# Revit family: OPUS-M
name_source: partatom
category: Mechanical Equipment
revit_build: Autodesk Revit 2015 (Build: 20140606_1530(x64)
units: mm (PartAtom-declared; Revit-internal decimal feet)

## types (2) — shared parameters
Catalogue Pages = http://www.nuaire.info
Discharge Spigot Diameter = 200 mm  [stored 0.656168 ft]
Electrical Phase = 1
Extract Spigot (Large) Diameter = 150 mm
Extract Spigot (Small) Diameter = 75 mm
Fax Number = +44(0)2920-858-222
Height = 233 mm  [stored 0.764436 ft]
I&M Manual = http://www.nuaire.info
IFCExportAs = IfcFanType
Length = 500 mm  [stored 1.64042 ft]
Manufacturer = Nuaire
Manufacturer Name = Nuaire
Maximum Ambient Temperature = 55 °C
Nominal Motor Rating = 0 W
Number of Connection Poles = 2
OmniClass Number = 23-33 31 19 13
OmniClass Title = Centrifugal Fans
Postcode = CF83 1NA
Revit Family Last Revised = 30/10/18
Telephone Number = +44(0)2920-858-200
URL = http://www.nuaire.co.uk
VAT Registration Number = 877308
Voltage = 230 V
Warranty Period = 3 Years
Weatherproof or Internal Only = Internal
Width = 330 mm

## per-type parameters (varying)
| type | Apparent Load | Classification.Uniclass.Pr.Description | Classification.Uniclass.Pr.Number | Description | Full Load Current | Starting Current | Unit Description | Weight |
| OPUS150-M | 179 VA | Centrifugal Fans | Pr_65_67_29_12 | Inline Single Extract Fan | 1 A | 1 A | Inline Single Extract Fan | 12.00 kg |
| OPUS100-2M | 90 VA | Twin centrifugal fans | Pr_65_67_29_89 | Inline Twin Extract Fan | 0 A | 0 A | Inline Twin Extract Fan | 11.00 kg |

note: column(s) folded — value = type name in every type: Model, Nuaire Model Code

note: [stored X ft] marks values corroborated as IEEE doubles in the binary element streams (Revit-internal decimal feet)

## geometry (parser evidence)
native form markers: Blend x22, Sweep x11
no freeform markers — native parametric forms only
